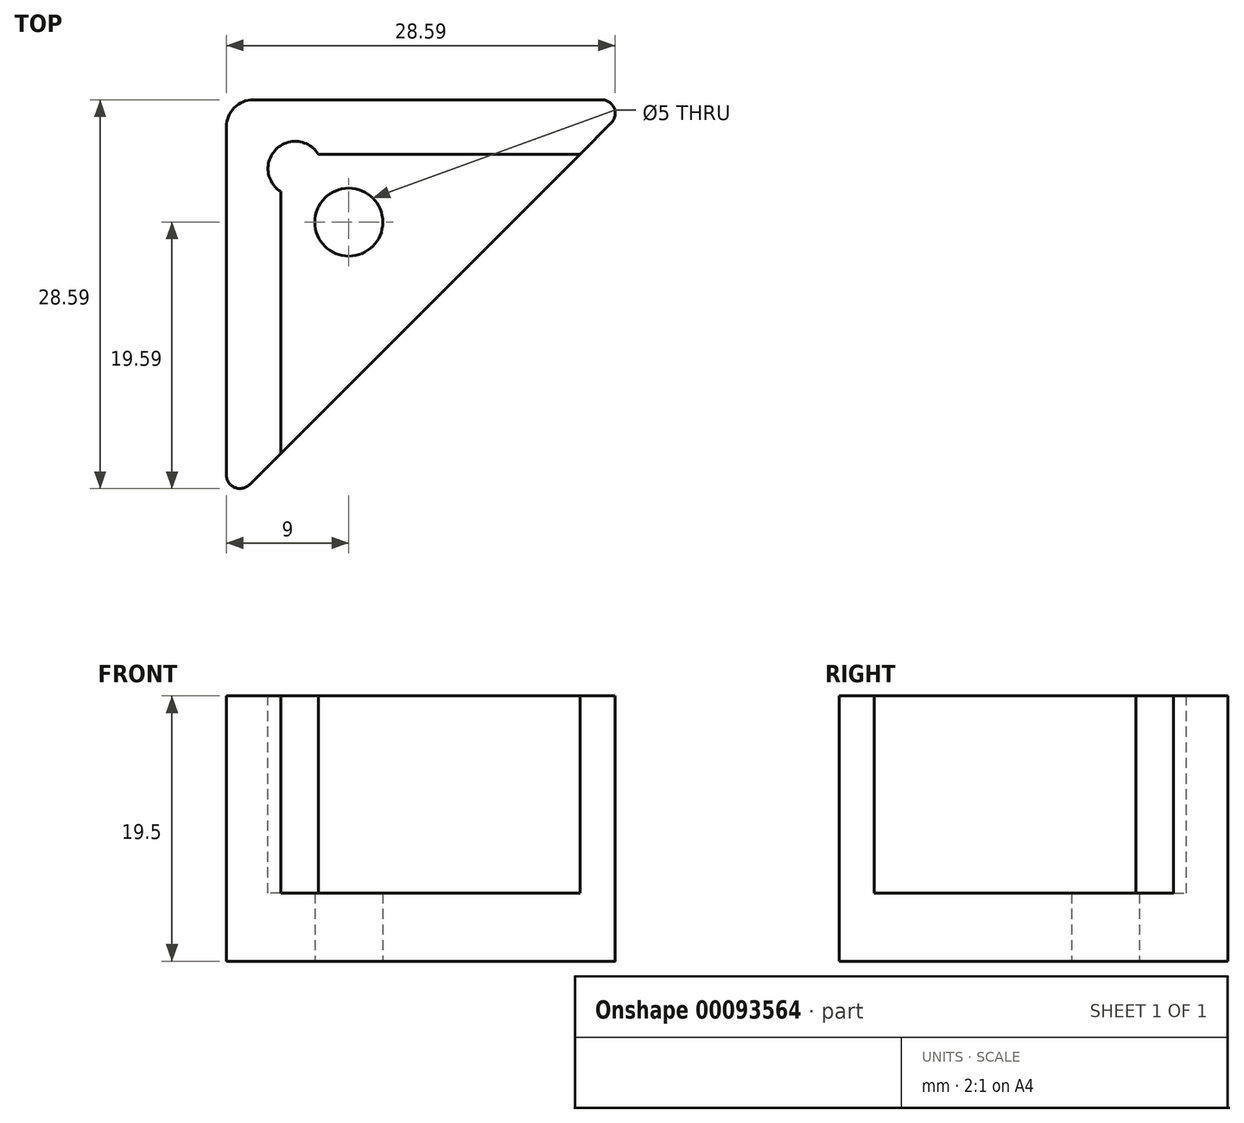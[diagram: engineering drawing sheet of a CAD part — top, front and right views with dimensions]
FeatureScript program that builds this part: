
annotation { "Feature Type Name" : "Feature", "Feature Type Description" : "" }
export const myFeature = defineFeature(function(context is Context, id is Id, definition is map)
    precondition{}
    {
        {
            var Q0;
            Q0=qCreatedBy(makeId("Top.planeOp"),FACE);
            var sketch = newSketch(context, id + "F0", { "sketchPlane" : qUnion([Q0])});
            skCircle(sketch, "E0", {"center": v(0, 0) * mm, "radius": 2.5 * mm});
            skLineSegment(sketch, "E1", {"start": v(-9, -21) * mm, "end": v(-9, 9) * mm});
            skLineSegment(sketch, "E2", {"start": v(-9, 9) * mm, "end": v(21, 9) * mm});
            skLineSegment(sketch, "E3", {"start": v(21, 9) * mm, "end": v(-9, -21) * mm});
            skSolve(sketch);
        }
        {
            var Q0;
            Q0 = qSketchRegion(id + "F0", true);
            extrude(context, id + "F1", {"entities" : qUnion([Q0]), "depth" : 5 * mm});
        }
        {
            var Q0;
            Q0=makeQuery(id+"F1.opExtrude","CAP_FACE",FACE,{"disambiguationData":[OSD([sQuery(id+"F0.wireOp",EDGE,"E0"),sQuery(id+"F0.wireOp",EDGE,"E1"),sQuery(id+"F0.wireOp",EDGE,"E2"),sQuery(id+"F0.wireOp",EDGE,"E3")])],"isStart":false});
            var sketch = newSketch(context, id + "F2", { "sketchPlane" : qUnion([Q0])});
            skLineSegment(sketch, "E4.0", {"start": v(-9, -21) * mm, "end": v(-9, 9) * mm});
            skLineSegment(sketch, "E5.0", {"start": v(-9, 9) * mm, "end": v(21, 9) * mm});
            skLineSegment(sketch, "E6", {"start": v(-9, -21) * mm, "end": v(-5, -17) * mm});
            skLineSegment(sketch, "E7", {"start": v(-5, -17) * mm, "end": v(-5, 5) * mm});
            skLineSegment(sketch, "E8", {"start": v(-5, 5) * mm, "end": v(17, 5) * mm});
            skLineSegment(sketch, "E9", {"start": v(17, 5) * mm, "end": v(21, 9) * mm});
            skSolve(sketch);
        }
        {
            var Q0;
            Q0 = qSketchRegion(id + "F2", true);
            extrude(context, id + "F3", {"entities" : qUnion([Q0]), "operationType" : NewBodyOperationType.ADD, "depth" : 14.5 * mm});
        }
        {
            var Q0;
            Q0=makeQuery(id+"F3.opExtrude","CAP_FACE",FACE,{"disambiguationData":[OSD([sQuery(id+"F2.wireOp",EDGE,"E4.0"),sQuery(id+"F2.wireOp",EDGE,"E5.0"),sQuery(id+"F2.wireOp",EDGE,"E6"),sQuery(id+"F2.wireOp",EDGE,"E7"),sQuery(id+"F2.wireOp",EDGE,"E8"),sQuery(id+"F2.wireOp",EDGE,"E9")])],"isStart":false});
            var sketch = newSketch(context, id + "F4", { "sketchPlane" : qUnion([Q0])});
            skLineSegment(sketch, "E10", {"start": v(-5, 5) * mm, "end": v(0, 0) * mm, "construction": true});
            skCircle(sketch, "E11", {"center": v(-3.94, 3.94) * mm, "radius": 2 * mm});
            skSolve(sketch);
        }
        {
            var Q0;
            Q0 = qSketchRegion(id + "F4", true);
            var Q1;
            Q1=makeQuery(id+"F1.opExtrude","CAP_FACE",FACE,{"disambiguationData":[OSD([sQuery(id+"F0.wireOp",EDGE,"E0"),sQuery(id+"F0.wireOp",EDGE,"E1"),sQuery(id+"F0.wireOp",EDGE,"E2"),sQuery(id+"F0.wireOp",EDGE,"E3")])],"isStart":false});
            extrude(context, id + "F5", {"entities" : qUnion([Q0]), "operationType" : NewBodyOperationType.REMOVE, "endBound" : BoundingType.UP_TO_SURFACE, "oppositeDirection" : true, "endBoundEntityFace" : qUnion([Q1]), "depth" : 25 * mm});
        }
        {
            var Q0;
            Q0=makeQuery(id+"F3.boolean.opBoolean","MERGE",EDGE,{"derivedFrom":[makeQuery(id+"F1.opExtrude","SWEPT_EDGE",EDGE,{"disambiguationData":[OSD([sQuery(id+"F0.wireOp",EDGE,"E2"),sQuery(id+"F0.wireOp",EDGE,"E3")])]}),makeQuery(id+"F3.opExtrude","SWEPT_EDGE",EDGE,{"disambiguationData":[OSD([sQuery(id+"F2.wireOp",EDGE,"E5.0"),sQuery(id+"F2.wireOp",EDGE,"E9")])]})]});
            fillet(context, id + "F6", {"entities" : qUnion([Q0]), "radius" : 1 * mm, "tangentPropagation" : true, "allowEdgeOverflow" : false});
        }
        {
            var Q0;
            Q0=makeQuery(id+"F3.boolean.opBoolean","MERGE",EDGE,{"derivedFrom":[makeQuery(id+"F1.opExtrude","SWEPT_EDGE",EDGE,{"disambiguationData":[OSD([sQuery(id+"F0.wireOp",EDGE,"E1"),sQuery(id+"F0.wireOp",EDGE,"E3")])]}),makeQuery(id+"F3.opExtrude","SWEPT_EDGE",EDGE,{"disambiguationData":[OSD([sQuery(id+"F2.wireOp",EDGE,"E4.0"),sQuery(id+"F2.wireOp",EDGE,"E6")])]})]});
            fillet(context, id + "F7", {"entities" : qUnion([Q0]), "radius" : 1 * mm, "tangentPropagation" : true, "allowEdgeOverflow" : false});
        }
        {
            var Q0;
            Q0=makeQuery(id+"F3.boolean.opBoolean","MERGE",EDGE,{"derivedFrom":[makeQuery(id+"F1.opExtrude","SWEPT_EDGE",EDGE,{"disambiguationData":[OSD([sQuery(id+"F0.wireOp",EDGE,"E1"),sQuery(id+"F0.wireOp",EDGE,"E2")])]}),makeQuery(id+"F3.opExtrude","SWEPT_EDGE",EDGE,{"disambiguationData":[OSD([sQuery(id+"F2.wireOp",EDGE,"E4.0"),sQuery(id+"F2.wireOp",EDGE,"E5.0")])]})]});
            fillet(context, id + "F8", {"entities" : qUnion([Q0]), "radius" : 2 * mm, "tangentPropagation" : true, "allowEdgeOverflow" : false});
        }
    });
